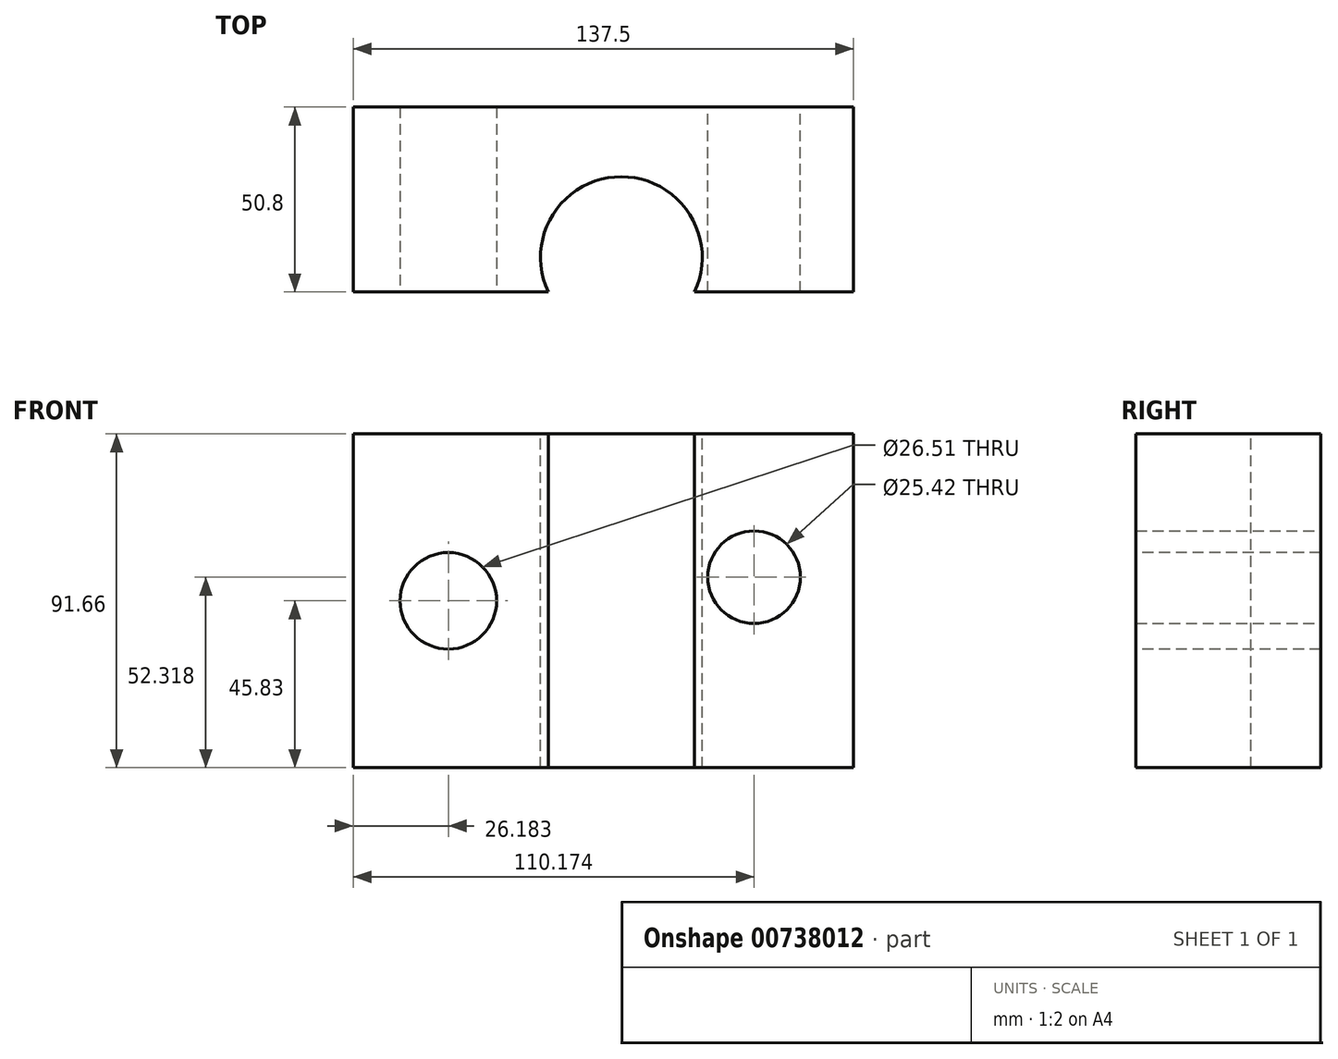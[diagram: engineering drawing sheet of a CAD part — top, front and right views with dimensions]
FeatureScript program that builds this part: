
annotation { "Feature Type Name" : "Feature", "Feature Type Description" : "" }
export const myFeature = defineFeature(function(context is Context, id is Id, definition is map)
    precondition{}
    {
        {
            var Q0;
            Q0=qCreatedBy(makeId("Front.planeOp"),FACE);
            var sketch = newSketch(context, id + "F0", { "sketchPlane" : qUnion([Q0])});
            skLineSegment(sketch, "E0.bottom", {"start": v(-68.75, 45.83) * mm, "end": v(68.75, 45.83) * mm});
            skLineSegment(sketch, "E0.top", {"start": v(-68.75, -45.83) * mm, "end": v(68.75, -45.83) * mm});
            skLineSegment(sketch, "E0.left", {"start": v(-68.75, 45.83) * mm, "end": v(-68.75, -45.83) * mm});
            skLineSegment(sketch, "E0.right", {"start": v(68.75, 45.83) * mm, "end": v(68.75, -45.83) * mm});
            skPoint(sketch, "E0.middle", {"position": v(0, 0) * mm});
            skSolve(sketch);
        }
        {
            var Q0;
            Q0 = qSketchRegion(id + "F0", true);
            extrude(context, id + "F1", {"entities" : qUnion([Q0]), "depth" : 76.2 * mm, "offsetDistance" : 25.4 * mm});
        }
        {
            var Q0;
            Q0=makeQuery(id+"F1.opExtrude","SWEPT_FACE",FACE,{"disambiguationData":[OSD([sQuery(id+"F0.wireOp",EDGE,"E0.bottom")])]});
            var sketch = newSketch(context, id + "F2", { "sketchPlane" : qUnion([Q0])});
            skSolve(sketch);
        }
        {
            var Q0;
            Q0=qCreatedBy(makeId("Front.planeOp"),FACE);
            var sketch = newSketch(context, id + "F3", { "sketchPlane" : qUnion([Q0])});
            skCircle(sketch, "E1", {"center": v(0, 31.92) * mm, "radius": 34.47 * mm});
            skSolve(sketch);
        }
        {
            var Q0;
            Q0 = qSketchRegion(id + "F3", true);
            extrude(context, id + "F4", {"entities" : qUnion([Q0]), "operationType" : NewBodyOperationType.REMOVE, "oppositeDirection" : true, "depth" : 76.2 * mm, "offsetDistance" : 25.4 * mm});
        }
        {
            var Q0;
            Q0=qCreatedBy(makeId("Front.planeOp"),FACE);
            var sketch = newSketch(context, id + "F5", { "sketchPlane" : qUnion([Q0])});
            skCircle(sketch, "E2", {"center": v(0, 32.82) * mm, "radius": 33.28 * mm});
            skSolve(sketch);
        }
        {
            var Q0;
            Q0 = qSketchRegion(id + "F5", true);
            var Q1;
            Q1=makeQuery(id+"F1.opExtrude","CAP_FACE",FACE,{"disambiguationData":[OSD([sQuery(id+"F0.wireOp",EDGE,"E0.bottom"),sQuery(id+"F0.wireOp",EDGE,"E0.top"),sQuery(id+"F0.wireOp",EDGE,"E0.left"),sQuery(id+"F0.wireOp",EDGE,"E0.right")])],"isStart":false});
            extrude(context, id + "F6", {"entities" : qUnion([Q0, Q1]), "operationType" : NewBodyOperationType.REMOVE, "oppositeDirection" : true, "depth" : 25.4 * mm, "offsetDistance" : 25.4 * mm});
        }
        {
            var Q0;
            Q0=qCreatedBy(makeId("Front.planeOp"),FACE);
            var sketch = newSketch(context, id + "F7", { "sketchPlane" : qUnion([Q0])});
            skCircle(sketch, "E3", {"center": v(0, 34.54) * mm, "radius": 29.7 * mm});
            skSolve(sketch);
        }
        {
            var Q0;
            Q0 = qSketchRegion(id + "F7", true);
            extrude(context, id + "F8", {"entities" : qUnion([Q0]), "operationType" : NewBodyOperationType.REMOVE, "oppositeDirection" : true, "depth" : 25.4 * mm, "offsetDistance" : 25.4 * mm});
        }
        {
            var Q0;
            Q0=qCreatedBy(makeId("Front.planeOp"),FACE);
            var sketch = newSketch(context, id + "F9", { "sketchPlane" : qUnion([Q0])});
            skCircle(sketch, "E4", {"center": v(0, 21.13) * mm, "radius": 24.82 * mm});
            skSolve(sketch);
        }
        {
            var Q0;
            Q0 = qSketchRegion(id + "F9", true);
            extrude(context, id + "F10", {"entities" : qUnion([Q0]), "operationType" : NewBodyOperationType.REMOVE, "oppositeDirection" : true, "depth" : 25.4 * mm, "offsetDistance" : 25.4 * mm});
        }
        {
            var Q0;
            {var subQ0=sQuery(id+"F0.wireOp",EDGE,"E0.bottom");Q0=makeQuery(id+"F2.imprint","IMPRINT",FACE,{"disambiguationData":[TD([[makeQuery(id+"F2.imprint","IMPRINT",EDGE,{"derivedFrom":makeQuery(id+"F1.opExtrude","CAP_EDGE",EDGE,{"disambiguationData":[OSD([subQ0])],"isStart":true})}),-1.0]])]});}
            var sketch = newSketch(context, id + "F11", { "sketchPlane" : qUnion([Q0])});
            skCircle(sketch, "E5", {"center": v(4.96, -41.35) * mm, "radius": 22.23 * mm});
            skSolve(sketch);
        }
        {
            var Q0;
            Q0 = qSketchRegion(id + "F11", true);
            extrude(context, id + "F12", {"entities" : qUnion([Q0]), "operationType" : NewBodyOperationType.REMOVE, "oppositeDirection" : true, "depth" : 127 * mm, "offsetDistance" : 25.4 * mm});
        }
        {
            var Q0;
            {var subQ0=sQuery(id+"F0.wireOp",EDGE,"E0.bottom");var subQ1=sQuery(id+"F0.wireOp",EDGE,"E0.top");var subQ2=sQuery(id+"F0.wireOp",EDGE,"E0.left");Q0=makeQuery(id+"F12.boolean.opBoolean","SPLIT",FACE,{"disambiguationData":[TD([makeQuery(id+"F1.opExtrude","SWEPT_FACE",FACE,{"disambiguationData":[OSD([subQ2])]})])],"derivedFrom":makeQuery(id+"F6.boolean.opBoolean","COPY",FACE,{"derivedFrom":makeQuery(id+"F6.opExtrude","CAP_FACE",FACE,{"disambiguationData":[OSD([subQ0,subQ1,subQ2,sQuery(id+"F0.wireOp",EDGE,"E0.right")])],"isStart":false})})});}
            var sketch = newSketch(context, id + "F13", { "sketchPlane" : qUnion([Q0])});
            skCircle(sketch, "E6", {"center": v(-42.57, 0) * mm, "radius": 13.26 * mm});
            skSolve(sketch);
        }
        {
            var Q0;
            Q0 = qSketchRegion(id + "F13", true);
            extrude(context, id + "F14", {"entities" : qUnion([Q0]), "operationType" : NewBodyOperationType.REMOVE, "oppositeDirection" : true, "depth" : 127 * mm, "offsetDistance" : 25.4 * mm});
        }
        {
            var Q0;
            Q0=qCreatedBy(makeId("Front.planeOp"),FACE);
            var sketch = newSketch(context, id + "F15", { "sketchPlane" : qUnion([Q0])});
            skCircle(sketch, "E7", {"center": v(51.03, 0) * mm, "radius": 12.33 * mm});
            skSolve(sketch);
        }
        {
            var Q0;
            Q0 = qSketchRegion(id + "F15", true);
            extrude(context, id + "F16", {"entities" : qUnion([Q0]), "operationType" : NewBodyOperationType.REMOVE, "oppositeDirection" : true, "depth" : 127 * mm, "offsetDistance" : 25.4 * mm});
        }
        {
            var Q0;
            Q0=qCreatedBy(makeId("Front.planeOp"),FACE);
            var sketch = newSketch(context, id + "F17", { "sketchPlane" : qUnion([Q0])});
            skCircle(sketch, "E8", {"center": v(48.1, 0) * mm, "radius": 13.73 * mm});
            skSolve(sketch);
        }
        {
            var Q0;
            Q0=makeQuery(id+"F17.imprint","IMPRINT",FACE,{"disambiguationData":[TD([[makeQuery(id+"F17.imprint","IMPRINT",EDGE,{"derivedFrom":sQuery(id+"F17.wireOp",EDGE,"E8")}),1.0]])]});
            var sketch = newSketch(context, id + "F18", { "sketchPlane" : qUnion([Q0])});
            skSolve(sketch);
        }
        {
            var Q0;
            Q0=makeQuery(id+"F17.imprint","IMPRINT",FACE,{"disambiguationData":[TD([[makeQuery(id+"F17.imprint","IMPRINT",EDGE,{"derivedFrom":sQuery(id+"F17.wireOp",EDGE,"E8")}),1.0]])]});
            extrude(context, id + "F19", {"entities" : qUnion([Q0]), "operationType" : NewBodyOperationType.REMOVE, "oppositeDirection" : true, "depth" : 127 * mm, "offsetDistance" : 25.4 * mm});
        }
        {
            var Q0;
            Q0=makeQuery(id+"F18.imprint","IMPRINT",FACE,{"disambiguationData":[TD([[makeQuery(id+"F18.imprint","IMPRINT",EDGE,{"derivedFrom":makeQuery(id+"F17.imprint","IMPRINT",EDGE,{"derivedFrom":sQuery(id+"F17.wireOp",EDGE,"E8")})}),1.0]])]});
            extrude(context, id + "F20", {"entities" : qUnion([Q0]), "operationType" : NewBodyOperationType.REMOVE, "oppositeDirection" : true, "depth" : 127 * mm, "offsetDistance" : 25.4 * mm});
        }
        {
            var Q0;
            Q0=qCreatedBy(makeId("Front.planeOp"),FACE);
            var sketch = newSketch(context, id + "F21", { "sketchPlane" : qUnion([Q0])});
            skCircle(sketch, "E9", {"center": v(40.08, 0) * mm, "radius": 15.1 * mm});
            skSolve(sketch);
        }
        {
            var Q0;
            Q0=makeQuery(id+"F21.imprint","IMPRINT",FACE,{"disambiguationData":[TD([[makeQuery(id+"F21.imprint","IMPRINT",EDGE,{"derivedFrom":sQuery(id+"F21.wireOp",EDGE,"E9")}),1.0]])]});
            extrude(context, id + "F22", {"entities" : qUnion([Q0]), "operationType" : NewBodyOperationType.REMOVE, "oppositeDirection" : true, "depth" : 127 * mm, "offsetDistance" : 25.4 * mm});
        }
        {
            var Q0;
            Q0=qCreatedBy(makeId("Front.planeOp"),FACE);
            var sketch = newSketch(context, id + "F23", { "sketchPlane" : qUnion([Q0])});
            skCircle(sketch, "E10", {"center": v(41.42, 6.49) * mm, "radius": 12.7 * mm});
            skSolve(sketch);
        }
        {
            var Q0;
            Q0 = qSketchRegion(id + "F23", true);
            extrude(context, id + "F24", {"entities" : qUnion([Q0]), "operationType" : NewBodyOperationType.REMOVE, "depth" : 152.4 * mm, "offsetDistance" : 25.4 * mm});
        }
    });
